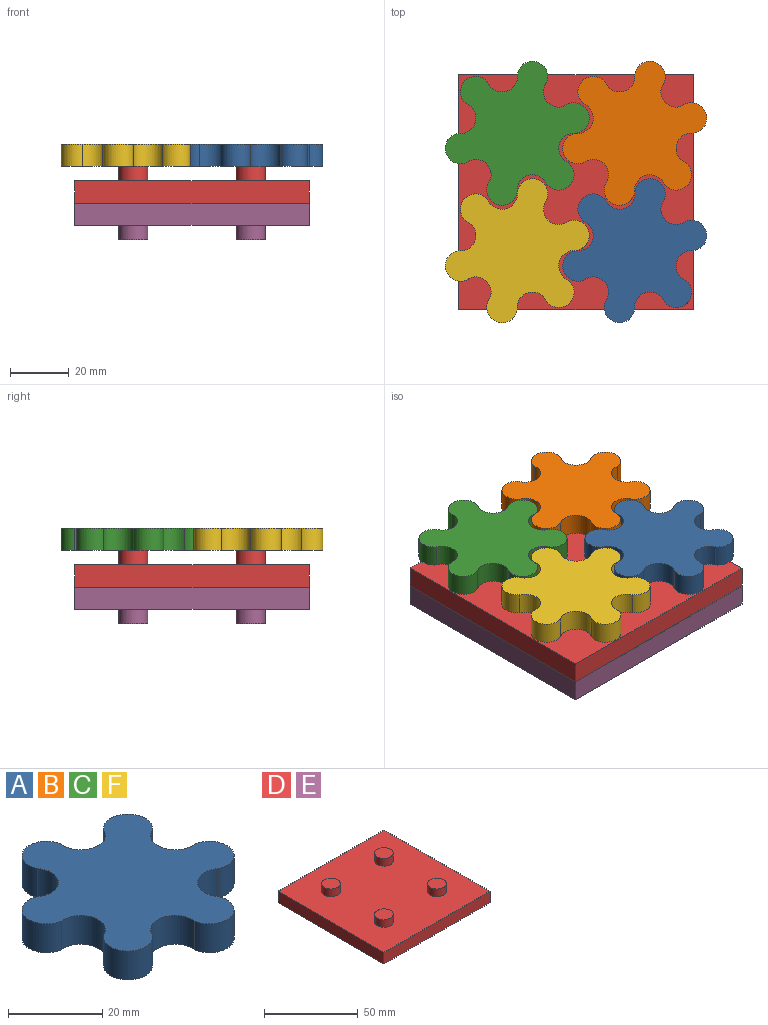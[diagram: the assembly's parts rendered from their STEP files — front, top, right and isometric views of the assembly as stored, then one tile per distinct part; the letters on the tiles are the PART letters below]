
ASSEMBLY  parts=6 mates=5
PART A: 14 faces, bbox 49.1x49.1x7.5 mm
  f0: cylinder r=5.22mm len=10.04mm, axis (0,0,-1), area 112.8mm2, adj f1,f11,f12,f13
  f1: cylinder r=5.22mm len=9.36mm, axis (0,0,-1), area 133.3mm2, adj f0,f2,f12,f13
  f2: cylinder r=5.22mm len=10.04mm, axis (0,0,-1), area 112.8mm2, adj f1,f3,f12,f13
  f3: cylinder r=5.22mm len=10.4mm, axis (0,0,-1), area 133.3mm2, adj f2,f4,f12,f13
  f4: cylinder r=5.22mm len=8.4mm, axis (0,0,-1), area 112.8mm2, adj f3,f5,f12,f13
  f5: cylinder r=5.22mm len=10.4mm, axis (0,0,-1), area 133.3mm2, adj f4,f6,f12,f13
  f6: cylinder r=5.22mm len=10.04mm, axis (0,0,-1), area 112.8mm2, adj f5,f7,f12,f13
  f7: cylinder r=5.22mm len=9.36mm, axis (0,0,-1), area 133.3mm2, adj f6,f8,f12,f13
  f8: cylinder r=5.22mm len=10.04mm, axis (0,0,-1), area 112.8mm2, adj f7,f9,f12,f13
  f9: cylinder r=5.22mm len=10.4mm, axis (0,0,-1), area 133.3mm2, adj f8,f10,f12,f13
  f10: cylinder r=5.22mm len=8.4mm, axis (0,0,-1), area 112.8mm2, adj f9,f11,f12,f13
  f11: cylinder r=5.22mm len=10.4mm, axis (0,0,-1), area 133.3mm2, adj f0,f10,f12,f13
  f12: plane 49.08x49.08mm, normal (0,0,1), area 1285.2mm2, adj f0,f1,f2,f3,f4,f5,f6,f7
  f13: plane 49.08x49.08mm, normal (0,0,-1), area 1285.2mm2, adj f0,f1,f2,f3,f4,f5,f6,f7
PART B: same geometry as A
PART C: same geometry as A
PART D: 14 faces, bbox 80x80x12.5 mm
  f0: plane 80x7.5mm, normal (0,1,0), area 600mm2, adj f1,f3,f4,f5
  f1: plane 80x7.5mm, normal (-1,0,0), area 600mm2, adj f0,f2,f4,f5
  f2: plane 80x7.5mm, normal (0,-1,0), area 600mm2, adj f1,f3,f4,f5
  f3: plane 80x7.5mm, normal (1,0,0), area 600mm2, adj f0,f2,f4,f5
  f4: plane 80x80mm, normal (0,0,1), area 6085.8mm2, adj f0,f1,f2,f3,f6,f8,f10,f12
  f5: plane 80x80mm, normal (0,0,-1), area 6400mm2, adj f0,f1,f2,f3
  f6: cylinder r=5mm len=10mm, axis (0,0,-1), area 157.1mm2, adj f4,f7
  f7: plane 10x10mm, normal (0,0,1), area 78.5mm2, adj f6
  f8: cylinder r=5mm len=10mm, axis (0,0,-1), area 157.1mm2, adj f4,f9
  f9: plane 10x10mm, normal (0,0,1), area 78.5mm2, adj f8
  f10: cylinder r=5mm len=10mm, axis (0,0,-1), area 157.1mm2, adj f4,f11
  f11: plane 10x10mm, normal (0,0,1), area 78.5mm2, adj f10
  f12: cylinder r=5mm len=10mm, axis (0,0,-1), area 157.1mm2, adj f4,f13
  f13: plane 10x10mm, normal (0,0,1), area 78.5mm2, adj f12
PART E: same geometry as D
PART F: same geometry as A
PLACE A rot(axis=(1,0,0),180deg) t=(105.22,-17.95,13.75)mm
PLACE B rot(axis=(1,0,0),180deg) t=(105.22,22.05,13.75)mm
PLACE C rot(axis=(1,0,0),180deg) t=(65.22,22.05,13.75)mm
PLACE D t=(85.22,2.05,-6.25)mm
PLACE E rot(axis=(1,0,0),180deg) t=(85.22,2.05,-6.25)mm
PLACE F rot(axis=(1,0,0),180deg) t=(65.22,-17.95,13.75)mm
MATE fastened E.f0 <-> D.f2  axis (0,-1,0) through (45.22,-37.95,-6.25)mm
MATE revolute A.f12 <-> D.f8  axis (0,0,-1) through (105.22,-17.95,6.25)mm
MATE revolute F.f12 <-> D.f6  axis (0,0,-1) through (65.22,-17.95,6.25)mm
MATE revolute C.f12 <-> D.f10  axis (0,0,-1) through (65.22,22.05,6.25)mm
MATE revolute B.f12 <-> D.f12  axis (0,0,-1) through (105.22,22.05,6.25)mm
